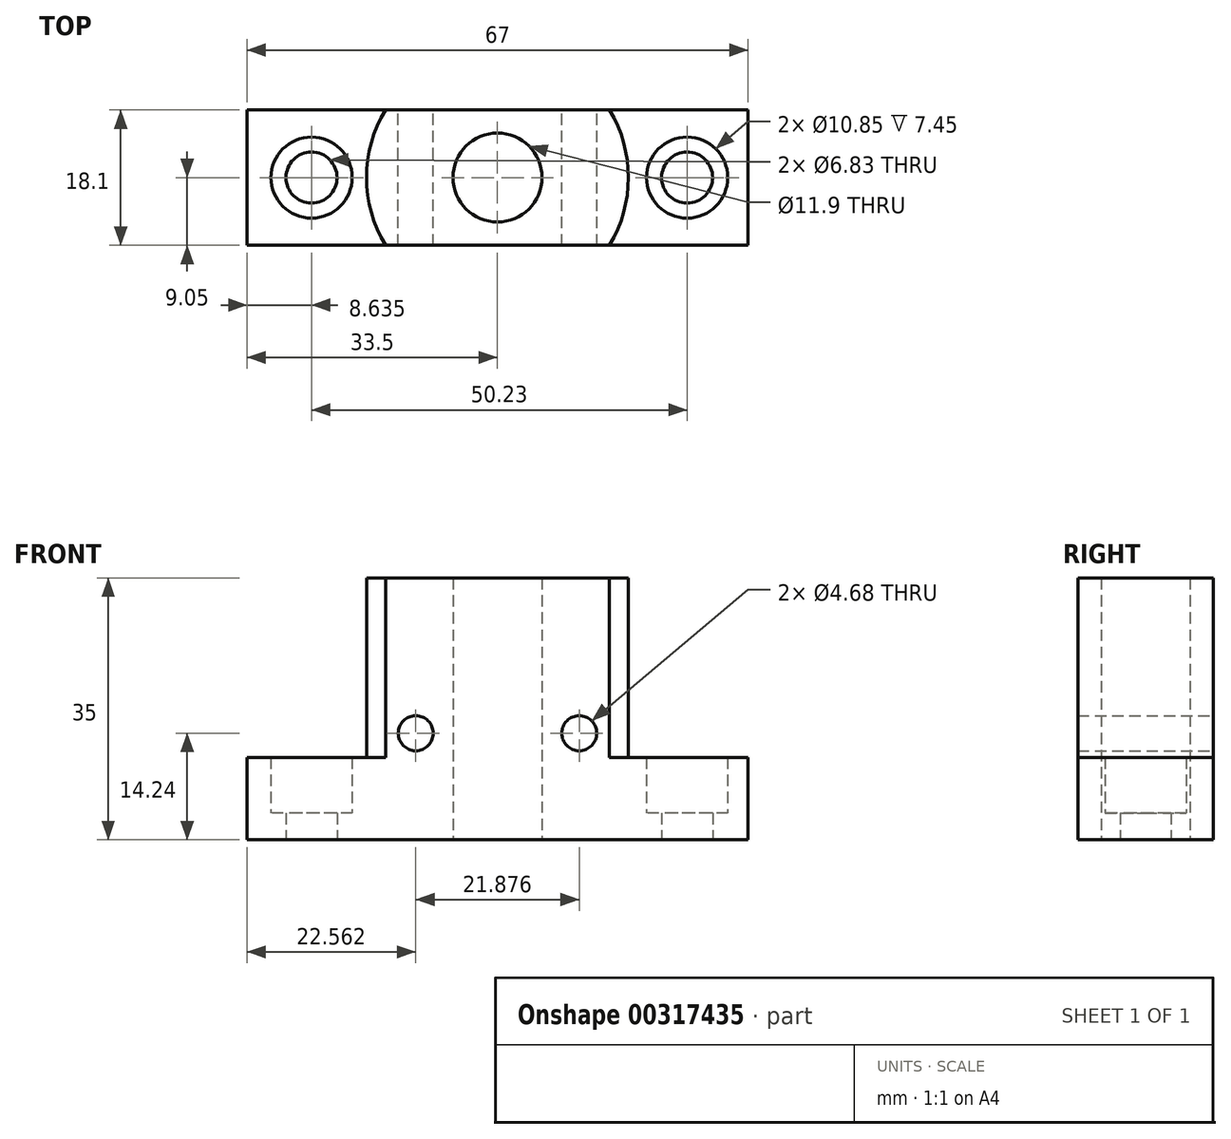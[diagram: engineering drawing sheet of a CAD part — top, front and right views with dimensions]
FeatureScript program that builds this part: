
annotation { "Feature Type Name" : "Feature", "Feature Type Description" : "" }
export const myFeature = defineFeature(function(context is Context, id is Id, definition is map)
    precondition{}
    {
        {
            var Q0;
            Q0=qCreatedBy(makeId("Top.planeOp"),FACE);
            var sketch = newSketch(context, id + "F0", { "sketchPlane" : qUnion([Q0])});
            skLineSegment(sketch, "E0.bottom", {"start": v(-33.5, 9.05) * mm, "end": v(33.5, 9.05) * mm});
            skLineSegment(sketch, "E0.top", {"start": v(-33.5, -9.05) * mm, "end": v(33.5, -9.05) * mm});
            skLineSegment(sketch, "E0.left", {"start": v(-33.5, 9.05) * mm, "end": v(-33.5, -9.05) * mm});
            skLineSegment(sketch, "E0.right", {"start": v(33.5, 9.05) * mm, "end": v(33.5, -9.05) * mm});
            skCircle(sketch, "E1", {"center": v(0, 0) * mm, "radius": 5.95 * mm});
            skCircle(sketch, "E2", {"center": v(25.37, 0) * mm, "radius": 3.42 * mm});
            skCircle(sketch, "E3", {"center": v(-24.87, 0) * mm, "radius": 3.42 * mm});
            skLineSegment(sketch, "E4.bottom", {"start": v(-14.98, 9.05) * mm, "end": v(14.98, 9.05) * mm});
            skLineSegment(sketch, "E4.top", {"start": v(-14.98, -9.05) * mm, "end": v(14.98, -9.05) * mm});
            skLineSegment(sketch, "E4.left", {"start": v(-14.98, 9.05) * mm, "end": v(-14.98, -9.05) * mm});
            skLineSegment(sketch, "E4.right", {"start": v(14.98, 9.05) * mm, "end": v(14.98, -9.05) * mm});
            skCircle(sketch, "E5", {"center": v(-24.87, 0) * mm, "radius": 5.42 * mm});
            skCircle(sketch, "E6", {"center": v(25.37, 0) * mm, "radius": 5.42 * mm});
            skCircle(sketch, "E7", {"center": v(0, 0) * mm, "radius": 17.5 * mm});
            skSolve(sketch);
        }
        {
            var Q0;
            Q0=makeQuery(id+"F0.imprint","IMPRINT",FACE,{"disambiguationData":[TD([[makeQuery(id+"F0.imprint","IMPRINT",EDGE,{"derivedFrom":sQuery(id+"F0.wireOp",EDGE,"E1")}),-1.0]])]});
            extrude(context, id + "F1", {"entities" : qUnion([Q0]), "depth" : 28 * mm});
        }
        {
            var Q0;
            {var subQ1=sQuery(id+"F0.wireOp",EDGE,"E0.left");Q0=makeQuery(id+"F0.imprint","IMPRINT",FACE,{"disambiguationData":[TD([[makeQuery(id+"F0.imprint","IMPRINT",EDGE,{"derivedFrom":subQ1}),1.0]])]});}
            var Q1;
            {var subQ1=sQuery(id+"F0.wireOp",EDGE,"E0.right");Q1=makeQuery(id+"F0.imprint","IMPRINT",FACE,{"disambiguationData":[TD([[makeQuery(id+"F0.imprint","IMPRINT",EDGE,{"derivedFrom":subQ1}),-1.0]])]});}
            extrude(context, id + "F2", {"entities" : qUnion([Q0, Q1]), "operationType" : NewBodyOperationType.ADD, "depth" : 11 * mm});
        }
        {
            var Q0;
            Q0=makeQuery(id+"F0.imprint","IMPRINT",FACE,{"disambiguationData":[TD([[makeQuery(id+"F0.imprint","IMPRINT",EDGE,{"derivedFrom":sQuery(id+"F0.wireOp",EDGE,"E3")}),-1.0]])]});
            var Q1;
            Q1=makeQuery(id+"F0.imprint","IMPRINT",FACE,{"disambiguationData":[TD([[makeQuery(id+"F0.imprint","IMPRINT",EDGE,{"derivedFrom":sQuery(id+"F0.wireOp",EDGE,"E2")}),-1.0]])]});
            extrude(context, id + "F3", {"entities" : qUnion([Q0, Q1]), "operationType" : NewBodyOperationType.ADD, "depth" : 3.55 * mm});
        }
        {
            var Q0;
            {var subQ0=sQuery(id+"F0.wireOp",EDGE,"E4.top");Q0=makeQuery(id+"F0.imprint","IMPRINT",FACE,{"disambiguationData":[TD([[makeQuery(id+"F0.imprint","IMPRINT",EDGE,{"derivedFrom":subQ0}),-1.0]])]});}
            var Q1;
            Q1=makeQuery(id+"F0.imprint","IMPRINT",FACE,{"disambiguationData":[TD([[makeQuery(id+"F0.imprint","IMPRINT",EDGE,{"derivedFrom":sQuery(id+"F0.wireOp",EDGE,"E1")}),-1.0]])]});
            var Q2;
            {var subQ0=sQuery(id+"F0.wireOp",EDGE,"E4.right");Q2=makeQuery(id+"F0.imprint","IMPRINT",FACE,{"disambiguationData":[TD([[makeQuery(id+"F0.imprint","IMPRINT",EDGE,{"derivedFrom":subQ0}),1.0]])]});}
            var Q3;
            {var subQ0=sQuery(id+"F0.wireOp",EDGE,"E4.bottom");Q3=makeQuery(id+"F0.imprint","IMPRINT",FACE,{"disambiguationData":[TD([[makeQuery(id+"F0.imprint","IMPRINT",EDGE,{"derivedFrom":subQ0}),1.0]])]});}
            var Q4;
            {var subQ0=sQuery(id+"F0.wireOp",EDGE,"E4.left");Q4=makeQuery(id+"F0.imprint","IMPRINT",FACE,{"disambiguationData":[TD([[makeQuery(id+"F0.imprint","IMPRINT",EDGE,{"derivedFrom":subQ0}),-1.0]])]});}
            extrude(context, id + "F4", {"entities" : qUnion([Q0, Q1, Q2, Q3, Q4]), "operationType" : NewBodyOperationType.ADD, "depth" : 35 * mm, "hasSecondDirection" : true, "secondDirectionOppositeDirection" : false, "secondDirectionDepth" : 27.9 * mm});
        }
        {
            var Q0;
            {var subQ0=sQuery(id+"F0.wireOp",EDGE,"E4.right");Q0=makeQuery(id+"F0.imprint","IMPRINT",FACE,{"disambiguationData":[TD([[makeQuery(id+"F0.imprint","IMPRINT",EDGE,{"derivedFrom":subQ0}),1.0]])]});}
            var Q1;
            {var subQ0=sQuery(id+"F0.wireOp",EDGE,"E4.left");Q1=makeQuery(id+"F0.imprint","IMPRINT",FACE,{"disambiguationData":[TD([[makeQuery(id+"F0.imprint","IMPRINT",EDGE,{"derivedFrom":subQ0}),-1.0]])]});}
            extrude(context, id + "F5", {"entities" : qUnion([Q0, Q1]), "operationType" : NewBodyOperationType.ADD, "depth" : 27.9 * mm});
        }
        {
            var Q0;
            Q0=qCreatedBy(makeId("Front.planeOp"),FACE);
            var sketch = newSketch(context, id + "F6", { "sketchPlane" : qUnion([Q0])});
            skLineSegment(sketch, "E8.bottom", {"start": v(-0.13, 35) * mm, "end": v(0.12, 35) * mm});
            skLineSegment(sketch, "E8.top", {"start": v(-0.12, 27.9) * mm, "end": v(0.13, 27.9) * mm});
            skLineSegment(sketch, "E8.left", {"start": v(-0.13, 35) * mm, "end": v(-0.12, 27.9) * mm});
            skLineSegment(sketch, "E8.right", {"start": v(0.12, 35) * mm, "end": v(0.13, 27.9) * mm});
            skSolve(sketch);
        }
        {
            var Q0;
            Q0=qSketchRegion(id+"F6",true);
            extrude(context, id + "F7", {"entities" : qUnion([Q0]), "operationType" : NewBodyOperationType.REMOVE, "oppositeDirection" : true, "depth" : 17.5 * mm, "hasSecondDirection" : true, "secondDirectionOppositeDirection" : true, "secondDirectionDepth" : 17.25 * mm});
        }
        {
            var Q0;
            {var subQ0=sQuery(id+"F0.wireOp",EDGE,"E4.bottom");var subQ1=sQuery(id+"F0.wireOp",EDGE,"E0.bottom");Q0=makeQuery(id+"F5.boolean.opBoolean","MERGE",FACE,{"derivedFrom":[makeQuery(id+"F2.opExtrude","SWEPT_FACE",FACE,{"disambiguationData":[OSD([subQ1]),TDD([makeQuery(id+"F0.imprint","IMPRINT",EDGE,{"disambiguationData":[TD([[makeQuery(id+"F0.imprint","INTERSECT",VERTEX,{"derivedFrom":[subQ1,sQuery(id+"F0.wireOp",EDGE,"E0.left")]}),-1.0]])],"derivedFrom":subQ1})])]}),makeQuery(id+"F2.opExtrude","SWEPT_FACE",FACE,{"disambiguationData":[OSD([subQ1]),TDD([makeQuery(id+"F0.imprint","IMPRINT",EDGE,{"disambiguationData":[TD([[makeQuery(id+"F0.imprint","INTERSECT",VERTEX,{"derivedFrom":[subQ1,sQuery(id+"F0.wireOp",EDGE,"E0.right")]}),1.0]])],"derivedFrom":subQ1})])]}),makeQuery(id+"F1.opExtrude","SWEPT_FACE",FACE,{"disambiguationData":[OSD([subQ0])]})]});}
            var sketch = newSketch(context, id + "F8", { "sketchPlane" : qUnion([Q0])});
            skCircle(sketch, "E9", {"center": v(-10.94, 14.24) * mm, "radius": 2.34 * mm});
            skCircle(sketch, "E10", {"center": v(10.94, 14.24) * mm, "radius": 2.34 * mm});
            skSolve(sketch);
        }
        {
            var Q0;
            Q0=makeQuery(id+"F8.imprint","IMPRINT",FACE,{"disambiguationData":[TD([[makeQuery(id+"F8.imprint","IMPRINT",EDGE,{"derivedFrom":sQuery(id+"F8.wireOp",EDGE,"E9")}),1.0]])]});
            var Q1;
            Q1=makeQuery(id+"F8.imprint","IMPRINT",FACE,{"disambiguationData":[TD([[makeQuery(id+"F8.imprint","IMPRINT",EDGE,{"derivedFrom":sQuery(id+"F8.wireOp",EDGE,"E10")}),1.0]])]});
            var Q2;
            Q2=sQuery(id+"F8.wireOp",EDGE,"E9");
            var Q3;
            Q3=sQuery(id+"F8.wireOp",EDGE,"E10");
            extrude(context, id + "F9", {"entities" : qUnion([Q0, Q1]), "operationType" : NewBodyOperationType.REMOVE, "surfaceEntities" : qUnion([Q2, Q3]), "endBound" : BoundingType.THROUGH_ALL, "oppositeDirection" : true, "depth" : 25 * mm});
        }
    });
